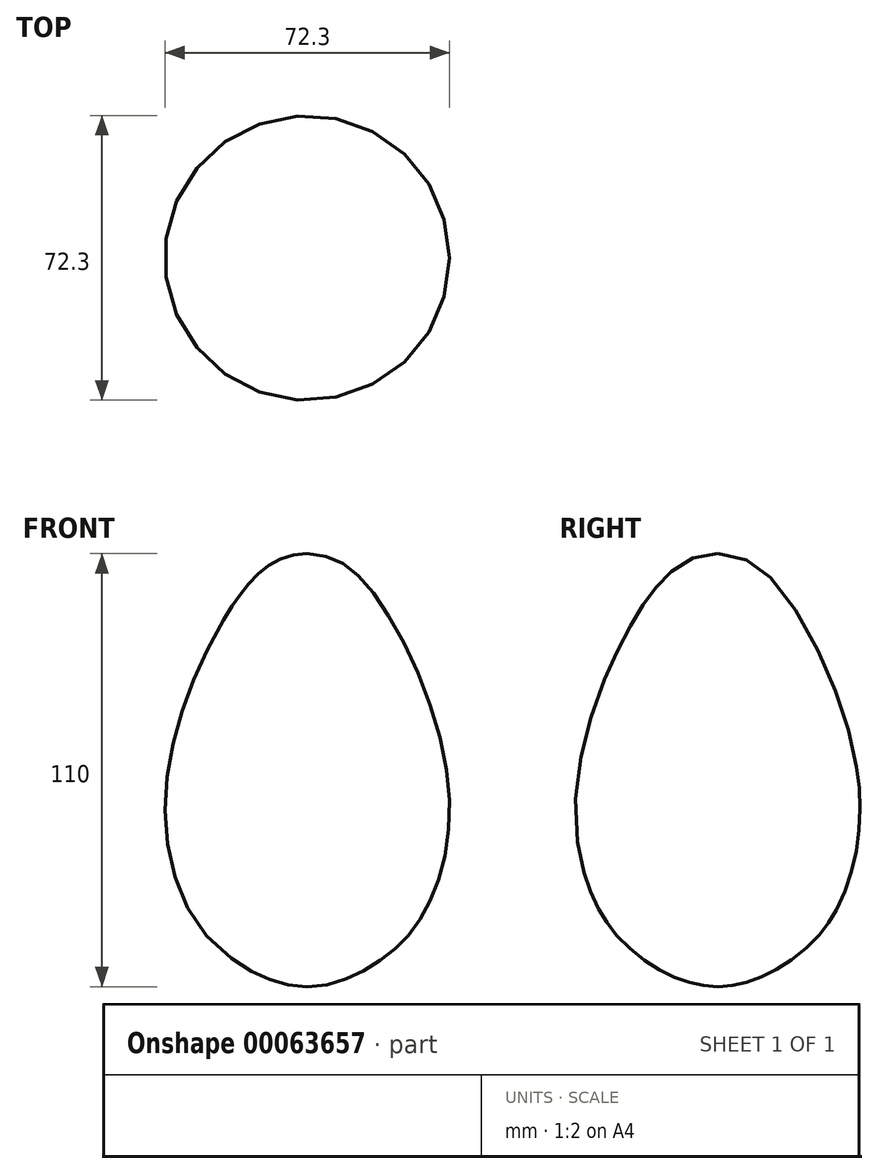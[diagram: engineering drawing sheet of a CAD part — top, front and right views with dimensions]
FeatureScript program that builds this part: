
annotation { "Feature Type Name" : "Feature", "Feature Type Description" : "" }
export const myFeature = defineFeature(function(context is Context, id is Id, definition is map)
    precondition{}
    {
        {
            var Q0;
            Q0=qCreatedBy(makeId("Front.planeOp"),FACE);
            var sketch = newSketch(context, id + "F0", { "sketchPlane" : qUnion([Q0])});
            skFitSpline(sketch, "E0", {"points": [v(0, 43.71) * mm, v(16, 34.71) * mm, v(35.5, -12) * mm, v(30.5, -46) * mm, v(18, -60) * mm, v(0, -66.29) * mm], "startDerivative": vector(119, -2.1) * mm, "endDerivative": vector(-116.3, 0) * mm});
            skLineSegment(sketch, "E1", {"start": v(0, -66.29) * mm, "end": v(0, 43.71) * mm});
            skSolve(sketch);
        }
        {
            var Q0;
            Q0=qSketchRegion(id+"F0",true);
            var Q1;
            Q1=sQuery(id+"F0.wireOp",EDGE,"E1");
            revolve(context, id + "F1", {"entities" : qUnion([Q0]), "axis" : qUnion([Q1]), "revolveType" : RevolveType.FULL});
        }
    });
